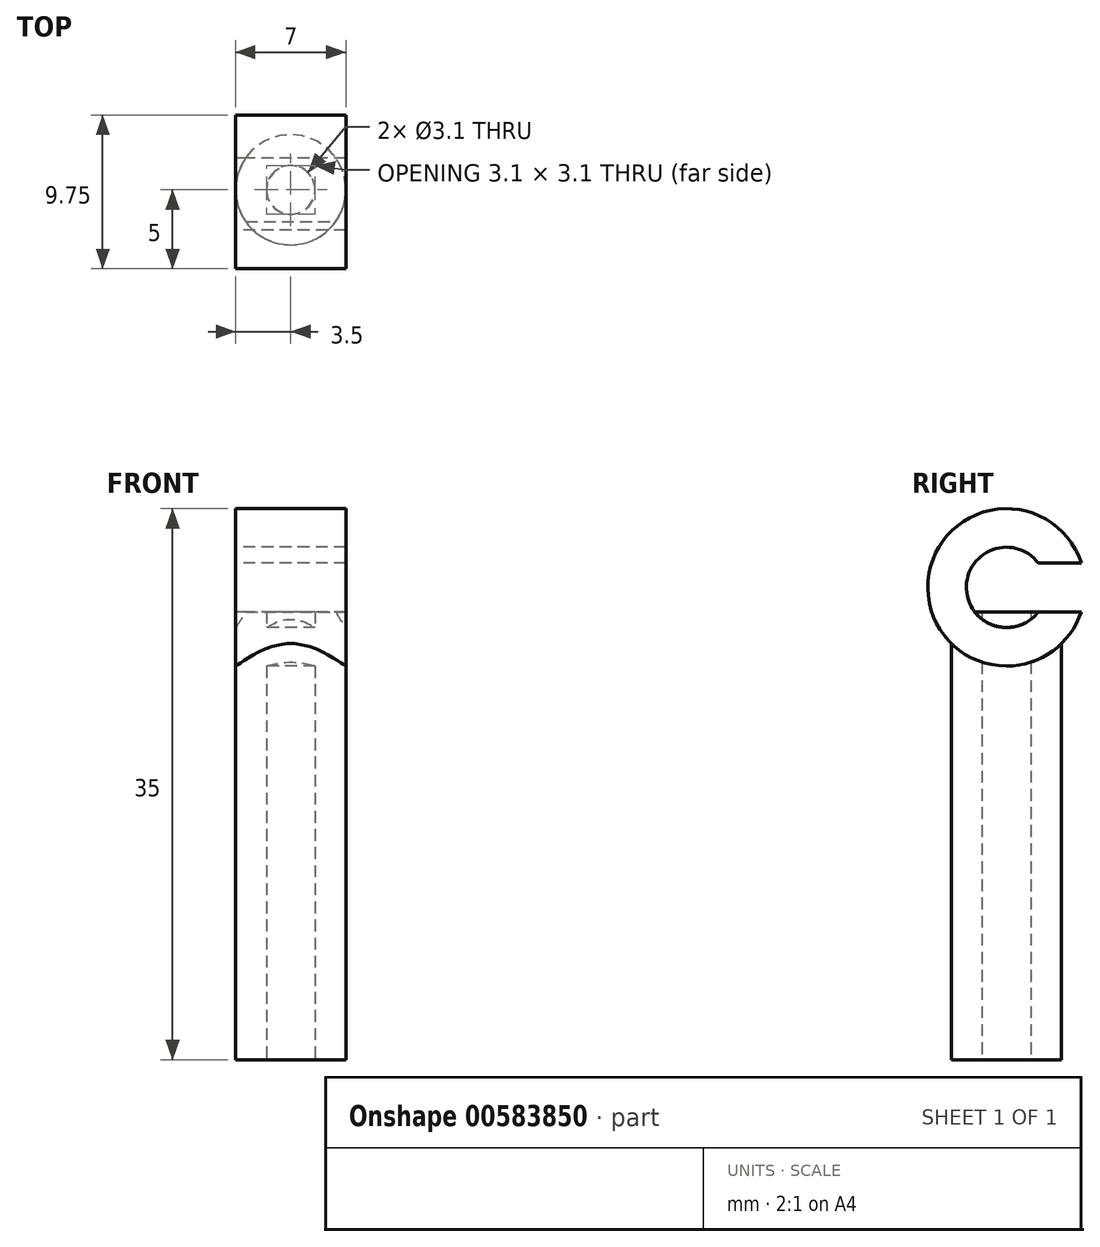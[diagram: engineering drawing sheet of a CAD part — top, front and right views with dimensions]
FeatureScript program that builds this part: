
annotation { "Feature Type Name" : "Feature", "Feature Type Description" : "" }
export const myFeature = defineFeature(function(context is Context, id is Id, definition is map)
    precondition{}
    {
        {
            var Q0;
            Q0=qCreatedBy(makeId("Top.planeOp"),FACE);
            var sketch = newSketch(context, id + "F0", { "sketchPlane" : qUnion([Q0])});
            skCircle(sketch, "E0", {"center": v(0, 0) * mm, "radius": 3.5 * mm});
            skCircle(sketch, "E1", {"center": v(0, 0) * mm, "radius": 1.55 * mm});
            skLineSegment(sketch, "E2.bottom", {"start": v(3.5, -3.5) * mm, "end": v(-3.5, -3.5) * mm});
            skLineSegment(sketch, "E2.top", {"start": v(3.5, 3.5) * mm, "end": v(-3.5, 3.5) * mm});
            skLineSegment(sketch, "E2.left", {"start": v(3.5, -3.5) * mm, "end": v(3.5, 3.5) * mm});
            skLineSegment(sketch, "E2.right", {"start": v(-3.5, -3.5) * mm, "end": v(-3.5, 3.5) * mm});
            skSolve(sketch);
        }
        {
            var Q0;
            Q0=makeQuery(id+"F0.imprint","IMPRINT",FACE,{"disambiguationData":[TD([[makeQuery(id+"F0.imprint","IMPRINT",EDGE,{"derivedFrom":sQuery(id+"F0.wireOp",EDGE,"E0")}),1.0]])]});
            extrude(context, id + "F1", {"entities" : qUnion([Q0]), "depth" : 20 * mm, "offsetDistance" : 25 * mm});
        }
        {
            var Q0;
            Q0=qCreatedBy(makeId("Right.planeOp"),FACE);
            var sketch = newSketch(context, id + "F2", { "sketchPlane" : qUnion([Q0])});
            skLineSegment(sketch, "E3", {"start": v(-3.5, 0) * mm, "end": v(-3.5, 16.43) * mm});
            skLineSegment(sketch, "E4.0", {"start": v(-3.5, 0) * mm, "end": v(3.5, 0) * mm});
            skCircle(sketch, "E5", {"center": v(0, 20) * mm, "radius": 5 * mm});
            skCircle(sketch, "E6", {"center": v(0, 20) * mm, "radius": 2.55 * mm});
            skLineSegment(sketch, "E7", {"start": v(3.5, 16.43) * mm, "end": v(3.5, 0) * mm});
            skLineSegment(sketch, "E8.bottom", {"start": v(6.64, 18.45) * mm, "end": v(-6.64, 18.45) * mm});
            skLineSegment(sketch, "E8.top", {"start": v(6.64, 21.55) * mm, "end": v(-6.64, 21.55) * mm});
            skLineSegment(sketch, "E8.left", {"start": v(6.64, 18.45) * mm, "end": v(6.64, 21.55) * mm});
            skLineSegment(sketch, "E8.right", {"start": v(-6.64, 18.45) * mm, "end": v(-6.64, 21.55) * mm});
            skSolve(sketch);
        }
        {
            var Q0;
            Q0=makeQuery(id+"F2.imprint","IMPRINT",FACE,{"disambiguationData":[TD([[makeQuery(id+"F2.imprint","IMPRINT",EDGE,{"derivedFrom":sQuery(id+"F2.wireOp",EDGE,"E6")}),-1.0]])]});
            var Q1;
            {var subQ0=sQuery(id+"F2.wireOp",EDGE,"E5");var subQ7=makeQuery(id+"F2.imprint","INTERSECT",VERTEX,{"derivedFrom":[sQuery(id+"F2.wireOp",EDGE,"E3"),subQ0]});Q1=makeQuery(id+"F2.imprint","IMPRINT",FACE,{"disambiguationData":[TD([[makeQuery(id+"F2.imprint","IMPRINT",EDGE,{"disambiguationData":[TD([[subQ7,1.0]])],"derivedFrom":subQ0}),1.0]])]});}
            extrude(context, id + "F3", {"entities" : qUnion([Q0, Q1]), "operationType" : NewBodyOperationType.ADD, "depth" : 7 * mm, "offsetDistance" : 25 * mm, "symmetric" : true});
        }
        {
            var Q0;
            Q0=makeQuery(id+"F2.imprint","IMPRINT",FACE,{"disambiguationData":[TD([[makeQuery(id+"F2.imprint","IMPRINT",EDGE,{"derivedFrom":sQuery(id+"F2.wireOp",EDGE,"E6")}),1.0]])]});
            extrude(context, id + "F4", {"entities" : qUnion([Q0]), "operationType" : NewBodyOperationType.REMOVE, "oppositeDirection" : true, "depth" : 25 * mm, "offsetDistance" : 25 * mm, "symmetric" : true});
        }
        {
            var Q0;
            {var subQ5=sQuery(id+"F2.wireOp",EDGE,"E8.left");Q0=makeQuery(id+"F2.imprint","IMPRINT",FACE,{"disambiguationData":[TD([[makeQuery(id+"F2.imprint","IMPRINT",EDGE,{"derivedFrom":subQ5}),1.0]])]});}
            var Q1;
            {var subQ0=sQuery(id+"F2.wireOp",EDGE,"E8.bottom");var subQ1=sQuery(id+"F2.wireOp",EDGE,"E6");var subQ2=makeQuery(id+"F2.imprint","INTERSECT",VERTEX,{"disambiguationData":[OD(0.0)],"derivedFrom":[subQ1,subQ0]});Q1=makeQuery(id+"F2.imprint","IMPRINT",FACE,{"disambiguationData":[TD([[makeQuery(id+"F2.imprint","IMPRINT",EDGE,{"disambiguationData":[TD([[subQ2,-1.0]])],"derivedFrom":subQ1}),1.0]])]});}
            var Q2;
            Q2=sQuery(id+"F2.wireOp",EDGE,"E6");
            extrude(context, id + "F5", {"entities" : qUnion([Q0, Q1]), "operationType" : NewBodyOperationType.REMOVE, "surfaceEntities" : qUnion([Q2]), "oppositeDirection" : true, "depth" : 25 * mm, "offsetDistance" : 25 * mm, "symmetric" : true});
        }
        {
            var Q0;
            Q0=qCreatedBy(makeId("Right.planeOp"),FACE);
            var sketch = newSketch(context, id + "F6", { "sketchPlane" : qUnion([Q0])});
            skArc(sketch, "E9.0.0", {"start": v(4.75, 18.45) * mm, "mid": v(5, 20) * mm, "end": v(4.75, 21.55) * mm});
            skLineSegment(sketch, "E9.0.1", {"start": v(4.75, 21.55) * mm, "end": v(2.02, 21.55) * mm});
            skArc(sketch, "E9.0.2", {"start": v(2.02, 21.55) * mm, "mid": v(2.55, 20) * mm, "end": v(2.02, 18.45) * mm});
            skLineSegment(sketch, "E9.0.3", {"start": v(2.02, 18.45) * mm, "end": v(4.75, 18.45) * mm});
            skLineSegment(sketch, "E10.0.0", {"start": v(4.75, 18.45) * mm, "end": v(6.64, 18.45) * mm});
            skLineSegment(sketch, "E10.0.1", {"start": v(6.64, 18.45) * mm, "end": v(6.64, 21.55) * mm});
            skLineSegment(sketch, "E10.0.2", {"start": v(6.64, 21.55) * mm, "end": v(4.75, 21.55) * mm});
            skArc(sketch, "E10.0.3", {"start": v(4.75, 21.55) * mm, "mid": v(5, 20) * mm, "end": v(4.75, 18.45) * mm});
            skLineSegment(sketch, "E11.0.0", {"start": v(-2.02, 18.45) * mm, "end": v(2.02, 18.45) * mm});
            skArc(sketch, "E11.0.1", {"start": v(2.02, 18.45) * mm, "mid": v(2.55, 20) * mm, "end": v(2.02, 21.55) * mm});
            skLineSegment(sketch, "E11.0.2", {"start": v(2.02, 21.55) * mm, "end": v(-2.02, 21.55) * mm});
            skArc(sketch, "E11.0.3", {"start": v(-2.02, 21.55) * mm, "mid": v(-2.55, 20) * mm, "end": v(-2.02, 18.45) * mm});
            skSolve(sketch);
        }
        {
            var Q0;
            Q0 = qSketchRegion(id + "F6", true);
            extrude(context, id + "F7", {"entities" : qUnion([Q0]), "operationType" : NewBodyOperationType.REMOVE, "oppositeDirection" : true, "depth" : 25 * mm, "offsetDistance" : 25 * mm, "symmetric" : true});
        }
        {
            var Q0;
            Q0=makeQuery(id+"F0.imprint","IMPRINT",FACE,{"disambiguationData":[TD([[makeQuery(id+"F0.imprint","IMPRINT",EDGE,{"derivedFrom":sQuery(id+"F0.wireOp",EDGE,"E1")}),-1.0]])]});
            extrude(context, id + "F8", {"entities" : qUnion([Q0]), "operationType" : NewBodyOperationType.ADD, "oppositeDirection" : true, "depth" : 10 * mm, "offsetDistance" : 25 * mm});
        }
    });
